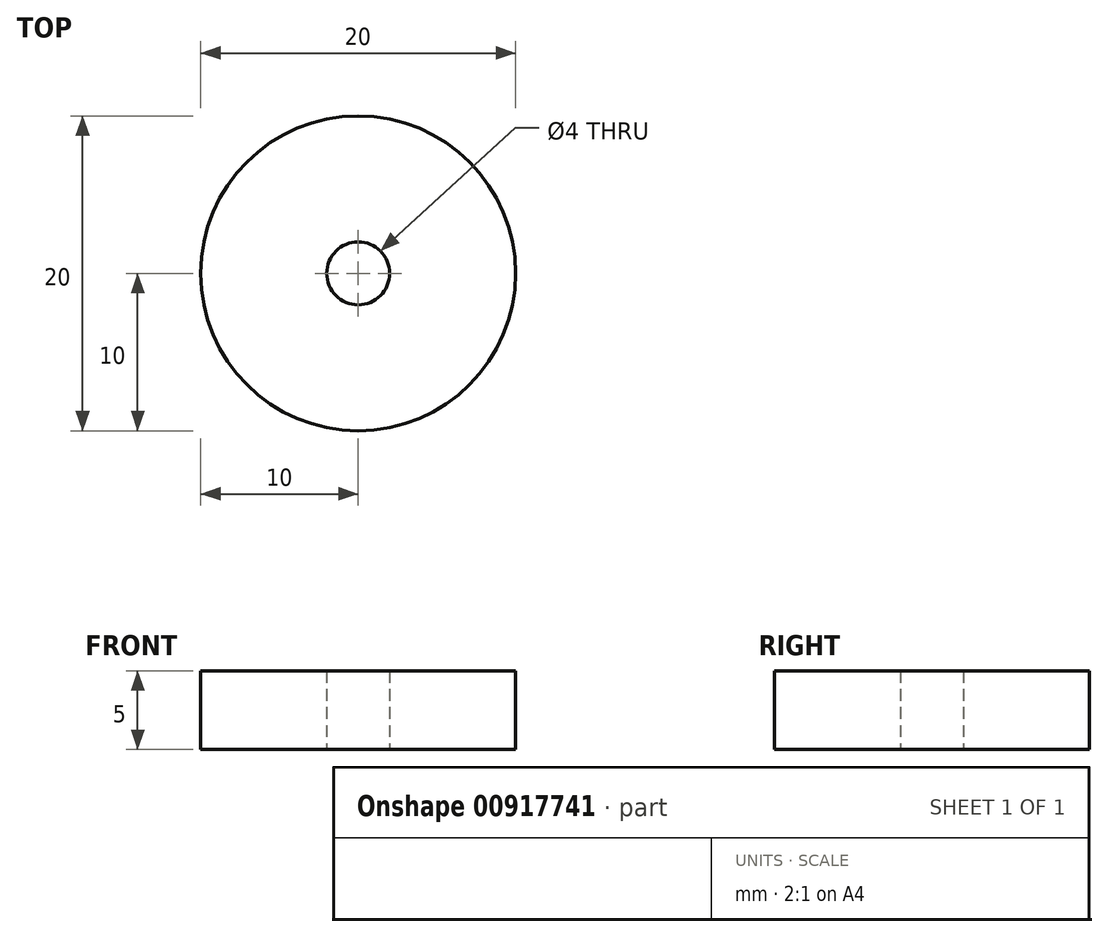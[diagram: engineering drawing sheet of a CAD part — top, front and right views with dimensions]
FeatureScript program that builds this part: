
annotation { "Feature Type Name" : "Feature", "Feature Type Description" : "" }
export const myFeature = defineFeature(function(context is Context, id is Id, definition is map)
    precondition{}
    {
        {
            var Q0;
            Q0=qCreatedBy(makeId("Top.planeOp"),FACE);
            var sketch = newSketch(context, id + "F0", { "sketchPlane" : qUnion([Q0])});
            skCircle(sketch, "E0", {"center": v(0, 0) * mm, "radius": 2 * mm});
            skCircle(sketch, "E1", {"center": v(0, 0) * mm, "radius": 10 * mm});
            skSolve(sketch);
        }
        {
            var Q0;
            Q0=makeQuery(id+"F0.imprint","IMPRINT",FACE,{"disambiguationData":[TD([[makeQuery(id+"F0.imprint","IMPRINT",EDGE,{"derivedFrom":sQuery(id+"F0.wireOp",EDGE,"E0")}),-1.0]])]});
            extrude(context, id + "F1", {"entities" : qUnion([Q0]), "depth" : 5 * mm, "offsetDistance" : 25 * mm});
        }
    });
